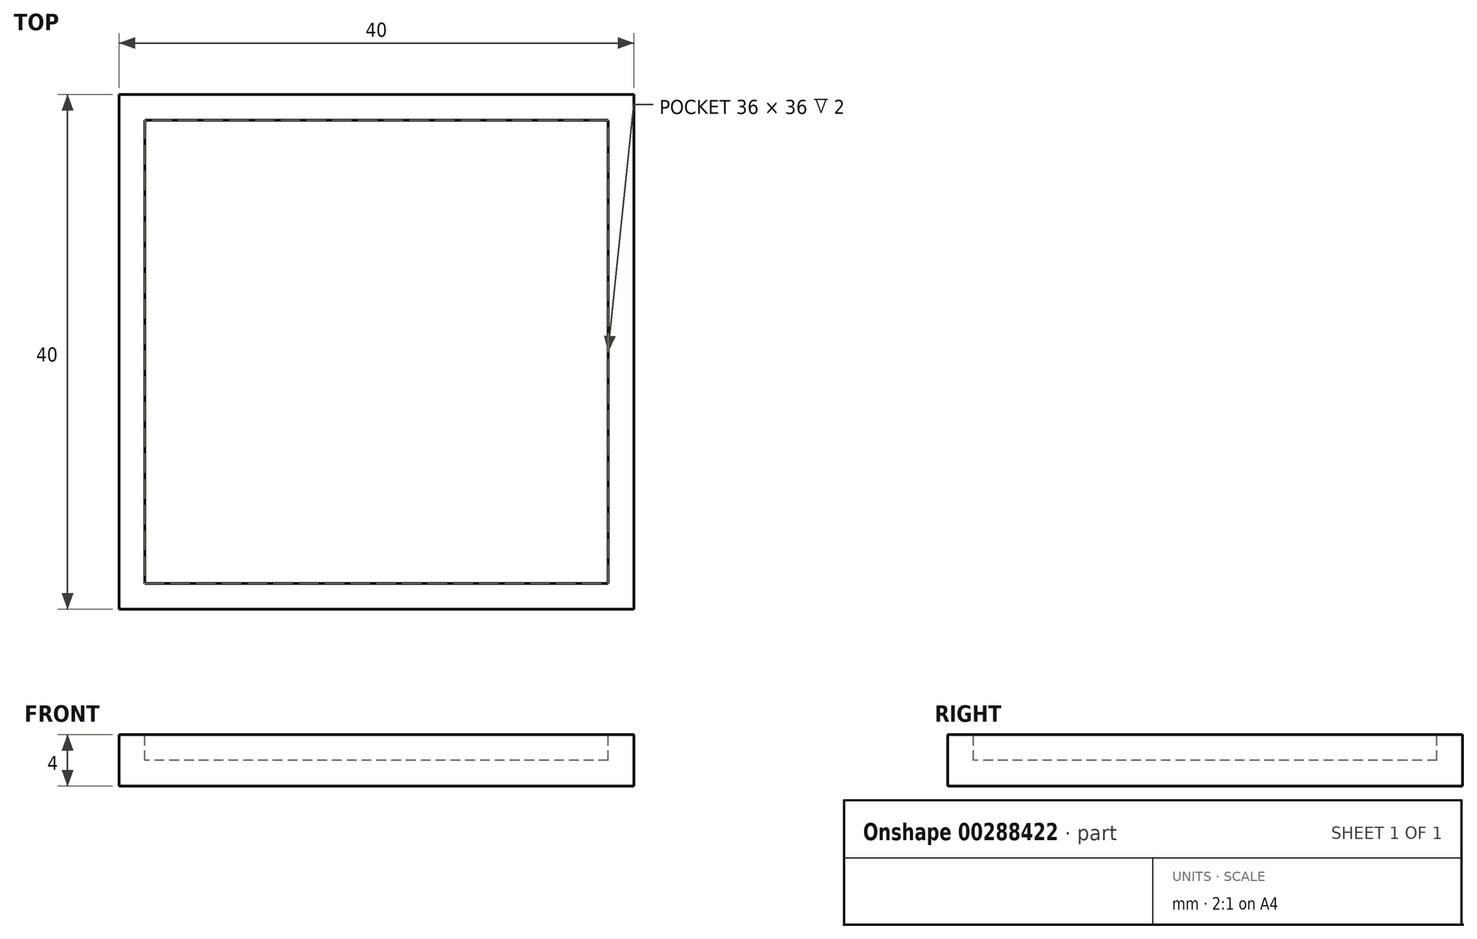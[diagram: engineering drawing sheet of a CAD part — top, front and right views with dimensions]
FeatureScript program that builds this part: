
annotation { "Feature Type Name" : "Feature", "Feature Type Description" : "" }
export const myFeature = defineFeature(function(context is Context, id is Id, definition is map)
    precondition{}
    {
        {
            var Q0;
            Q0=qCreatedBy(makeId("Top.planeOp"),FACE);
            var sketch = newSketch(context, id + "F0", { "sketchPlane" : qUnion([Q0])});
            skLineSegment(sketch, "E0.bottom", {"start": v(-21.69, 21.94) * mm, "end": v(18.31, 21.94) * mm});
            skLineSegment(sketch, "E0.top", {"start": v(-21.69, -18.06) * mm, "end": v(18.31, -18.06) * mm});
            skLineSegment(sketch, "E0.left", {"start": v(-21.69, 21.94) * mm, "end": v(-21.69, -18.06) * mm});
            skLineSegment(sketch, "E0.right", {"start": v(18.31, 21.94) * mm, "end": v(18.31, -18.06) * mm});
            skSolve(sketch);
        }
        {
            var Q0;
            Q0 = qSketchRegion(id + "F0", true);
            extrude(context, id + "F1", {"entities" : qUnion([Q0]), "depth" : 4 * mm});
        }
        {
            var Q0;
            Q0=makeQuery(id+"F1.opExtrude","CAP_FACE",FACE,{"disambiguationData":[OSD([sQuery(id+"F0.wireOp",EDGE,"E0.bottom"),sQuery(id+"F0.wireOp",EDGE,"E0.top"),sQuery(id+"F0.wireOp",EDGE,"E0.left"),sQuery(id+"F0.wireOp",EDGE,"E0.right")])],"isStart":false});
            var sketch = newSketch(context, id + "F2", { "sketchPlane" : qUnion([Q0])});
            skLineSegment(sketch, "E1.0", {"start": v(-19.69, 19.94) * mm, "end": v(-19.69, -16.06) * mm});
            skLineSegment(sketch, "E1.1", {"start": v(16.31, 19.94) * mm, "end": v(-19.69, 19.94) * mm});
            skLineSegment(sketch, "E1.2", {"start": v(16.31, -16.06) * mm, "end": v(16.31, 19.94) * mm});
            skLineSegment(sketch, "E1.3", {"start": v(-19.69, -16.06) * mm, "end": v(16.31, -16.06) * mm});
            skSolve(sketch);
        }
        {
            var Q0;
            Q0=makeQuery(id+"F2.imprint","IMPRINT",FACE,{"disambiguationData":[TD([[makeQuery(id+"F2.imprint","IMPRINT",EDGE,{"derivedFrom":sQuery(id+"F2.wireOp",EDGE,"E1.0")}),1.0]])]});
            extrude(context, id + "F3", {"entities" : qUnion([Q0]), "operationType" : NewBodyOperationType.ADD, "oppositeDirection" : true, "depth" : 2 * mm});
        }
        {
            var Q0;
            Q0=makeQuery(id+"F1.opExtrude","CAP_FACE",FACE,{"disambiguationData":[OSD([sQuery(id+"F0.wireOp",EDGE,"E0.bottom"),sQuery(id+"F0.wireOp",EDGE,"E0.top"),sQuery(id+"F0.wireOp",EDGE,"E0.left"),sQuery(id+"F0.wireOp",EDGE,"E0.right")])],"isStart":false});
            var sketch = newSketch(context, id + "F4", { "sketchPlane" : qUnion([Q0])});
            skLineSegment(sketch, "E2.0", {"start": v(-19.69, 19.94) * mm, "end": v(-19.69, -16.06) * mm});
            skLineSegment(sketch, "E2.1", {"start": v(16.31, 19.94) * mm, "end": v(-19.69, 19.94) * mm});
            skLineSegment(sketch, "E2.2", {"start": v(16.31, -16.06) * mm, "end": v(16.31, 19.94) * mm});
            skLineSegment(sketch, "E2.3", {"start": v(-19.69, -16.06) * mm, "end": v(16.31, -16.06) * mm});
            skSolve(sketch);
        }
        {
            var Q0;
            Q0=makeQuery(id+"F4.imprint","IMPRINT",FACE,{"disambiguationData":[TD([[makeQuery(id+"F4.imprint","IMPRINT",EDGE,{"derivedFrom":sQuery(id+"F4.wireOp",EDGE,"E2.0")}),1.0]])]});
            extrude(context, id + "F5", {"entities" : qUnion([Q0]), "operationType" : NewBodyOperationType.REMOVE, "oppositeDirection" : true, "depth" : 2 * mm});
        }
    });
